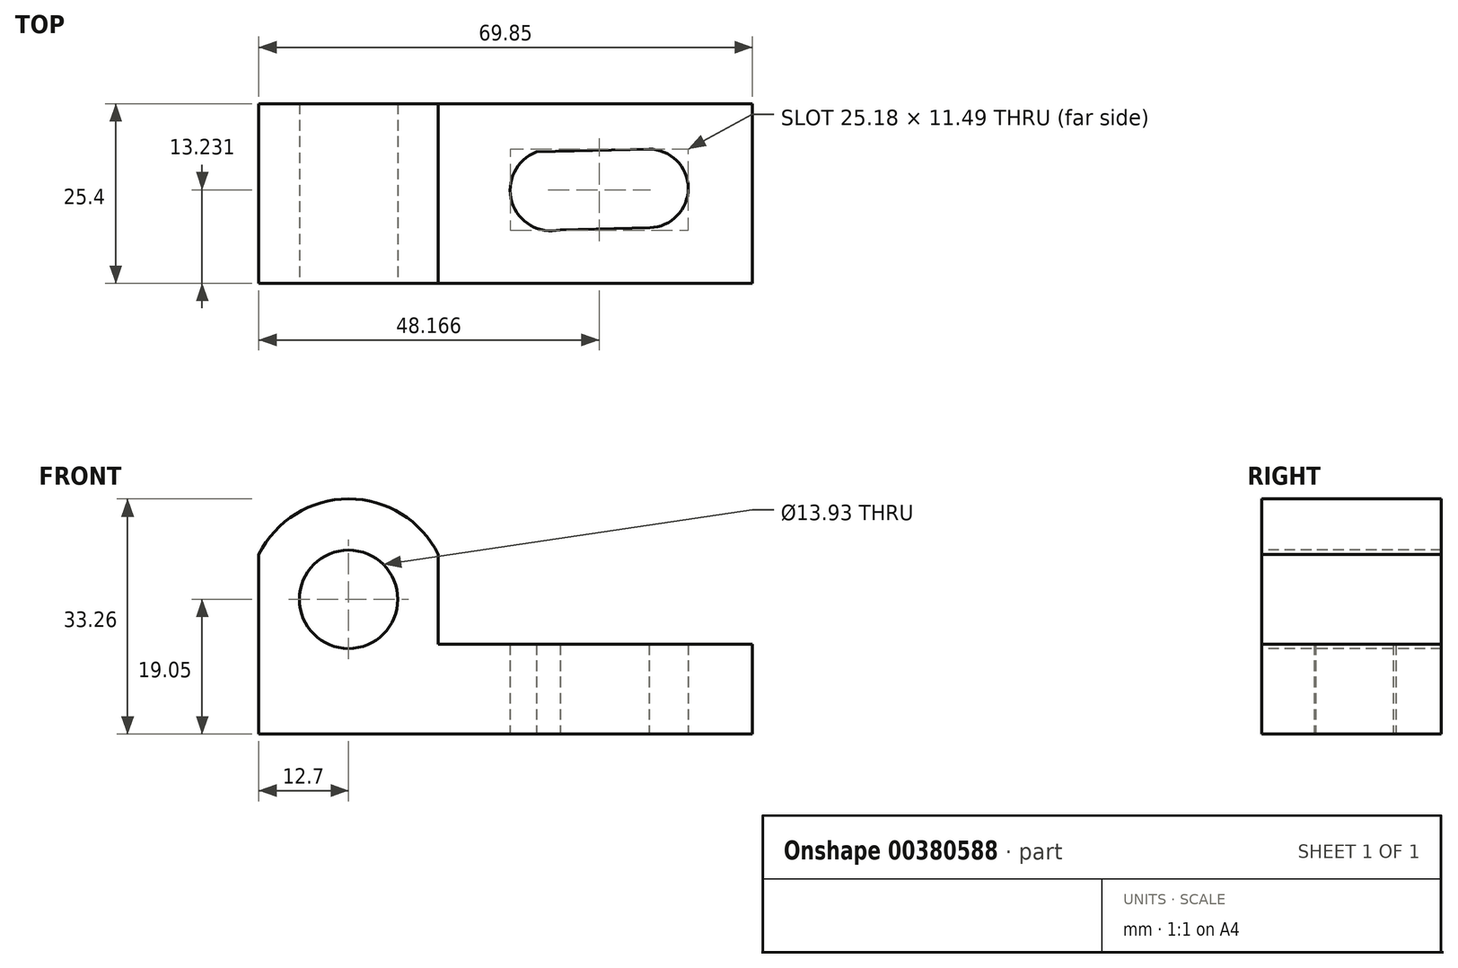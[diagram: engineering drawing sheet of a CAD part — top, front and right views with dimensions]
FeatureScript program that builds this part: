
annotation { "Feature Type Name" : "Feature", "Feature Type Description" : "" }
export const myFeature = defineFeature(function(context is Context, id is Id, definition is map)
    precondition{}
    {
        {
            var Q0;
            Q0=qCreatedBy(makeId("Front.planeOp"),FACE);
            var sketch = newSketch(context, id + "F0", { "sketchPlane" : qUnion([Q0])});
            skLineSegment(sketch, "E0", {"start": v(0, 0) * mm, "end": v(0, 38.1) * mm});
            skLineSegment(sketch, "E1", {"start": v(0, 38.1) * mm, "end": v(25.4, 38.1) * mm});
            skLineSegment(sketch, "E2", {"start": v(25.4, 38.1) * mm, "end": v(25.4, 12.7) * mm});
            skLineSegment(sketch, "E3", {"start": v(25.4, 12.7) * mm, "end": v(69.85, 12.7) * mm});
            skLineSegment(sketch, "E4", {"start": v(69.85, 12.7) * mm, "end": v(69.85, 0) * mm});
            skLineSegment(sketch, "E5", {"start": v(69.85, 0) * mm, "end": v(0, 0) * mm});
            skSolve(sketch);
        }
        {
            var Q0;
            Q0=makeQuery(id+"F0.imprint","IMPRINT",FACE,{"disambiguationData":[TD([[makeQuery(id+"F0.imprint","IMPRINT",EDGE,{"derivedFrom":sQuery(id+"F0.wireOp",EDGE,"E0")}),-1.0]])]});
            extrude(context, id + "F1", {"entities" : qUnion([Q0]), "depth" : 25.4 * mm});
        }
        {
            var Q0;
            Q0=makeQuery(id+"F1.opExtrude","CAP_FACE",FACE,{"disambiguationData":[OSD([sQuery(id+"F0.wireOp",EDGE,"E0"),sQuery(id+"F0.wireOp",EDGE,"E1"),sQuery(id+"F0.wireOp",EDGE,"E2"),sQuery(id+"F0.wireOp",EDGE,"E3"),sQuery(id+"F0.wireOp",EDGE,"E4"),sQuery(id+"F0.wireOp",EDGE,"E5")])],"isStart":false});
            var sketch = newSketch(context, id + "F2", { "sketchPlane" : qUnion([Q0])});
            skPoint(sketch, "E6.centerSnap0", {"position": v(25.4, 25.4) * mm});
            skCircle(sketch, "E7", {"center": v(12.7, 19.05) * mm, "radius": 6.96 * mm});
            skPoint(sketch, "E7.centerSnap0", {"position": v(12.7, 38.1) * mm});
            skArc(sketch, "E8", {"start": v(25.4, 25.4) * mm, "mid": v(12.7, 33.26) * mm, "end": v(0, 25.4) * mm});
            skSolve(sketch);
        }
        {
            var Q0;
            Q0=makeQuery(id+"F2.imprint","IMPRINT",FACE,{"disambiguationData":[TD([[makeQuery(id+"F2.imprint","IMPRINT",EDGE,{"derivedFrom":sQuery(id+"F2.wireOp",EDGE,"E7")}),1.0]])]});
            var Q1;
            {var subQ0=sQuery(id+"F2.wireOp",EDGE,"E8");Q1=makeQuery(id+"F2.imprint","IMPRINT",FACE,{"disambiguationData":[TD([[makeQuery(id+"F2.imprint","IMPRINT",EDGE,{"derivedFrom":subQ0}),-1.0]])]});}
            extrude(context, id + "F3", {"entities" : qUnion([Q0, Q1]), "operationType" : NewBodyOperationType.REMOVE, "oppositeDirection" : true, "depth" : 25.4 * mm});
        }
        {
            var Q0;
            Q0=qCreatedBy(makeId("Top.planeOp"),FACE);
            var sketch = newSketch(context, id + "F4", { "sketchPlane" : qUnion([Q0])});
            skCircle(sketch, "E9", {"center": v(41.3, -12.22) * mm, "radius": 5.75 * mm});
            skCircle(sketch, "E10", {"center": v(55.2, -11.98) * mm, "radius": 5.56 * mm});
            skLineSegment(sketch, "E11", {"start": v(42.63, -17.82) * mm, "end": v(55.33, -17.53) * mm});
            skLineSegment(sketch, "E12", {"start": v(55.2, -6.42) * mm, "end": v(39.3, -6.83) * mm});
            skArc(sketch, "E13", {"start": v(63.5, -24.6) * mm, "mid": v(67.69, -12.3) * mm, "end": v(63.5, 0) * mm});
            skSolve(sketch);
        }
        {
            var Q0;
            {var subQ0=sQuery(id+"F4.wireOp",EDGE,"E11");Q0=makeQuery(id+"F4.imprint","IMPRINT",FACE,{"disambiguationData":[TD([[makeQuery(id+"F4.imprint","IMPRINT",EDGE,{"derivedFrom":subQ0}),1.0]])]});}
            var Q1;
            {var subQ0=sQuery(id+"F4.wireOp",EDGE,"E10");var subQ1=makeQuery(id+"F4.imprint","INTERSECT",VERTEX,{"derivedFrom":[subQ0,sQuery(id+"F4.wireOp",EDGE,"E11")]});Q1=makeQuery(id+"F4.imprint","IMPRINT",FACE,{"disambiguationData":[TD([[makeQuery(id+"F4.imprint","IMPRINT",EDGE,{"disambiguationData":[TD([[subQ1,1.0]])],"derivedFrom":subQ0}),1.0]])]});}
            var Q2;
            {var subQ0=sQuery(id+"F4.wireOp",EDGE,"E9");var subQ1=makeQuery(id+"F4.imprint","INTERSECT",VERTEX,{"derivedFrom":[subQ0,sQuery(id+"F4.wireOp",EDGE,"E11")]});Q2=makeQuery(id+"F4.imprint","IMPRINT",FACE,{"disambiguationData":[TD([[makeQuery(id+"F4.imprint","IMPRINT",EDGE,{"disambiguationData":[TD([[subQ1,1.0]])],"derivedFrom":subQ0}),1.0]])]});}
            extrude(context, id + "F5", {"entities" : qUnion([Q0, Q1, Q2]), "operationType" : NewBodyOperationType.REMOVE, "depth" : 12.7 * mm});
        }
    });
